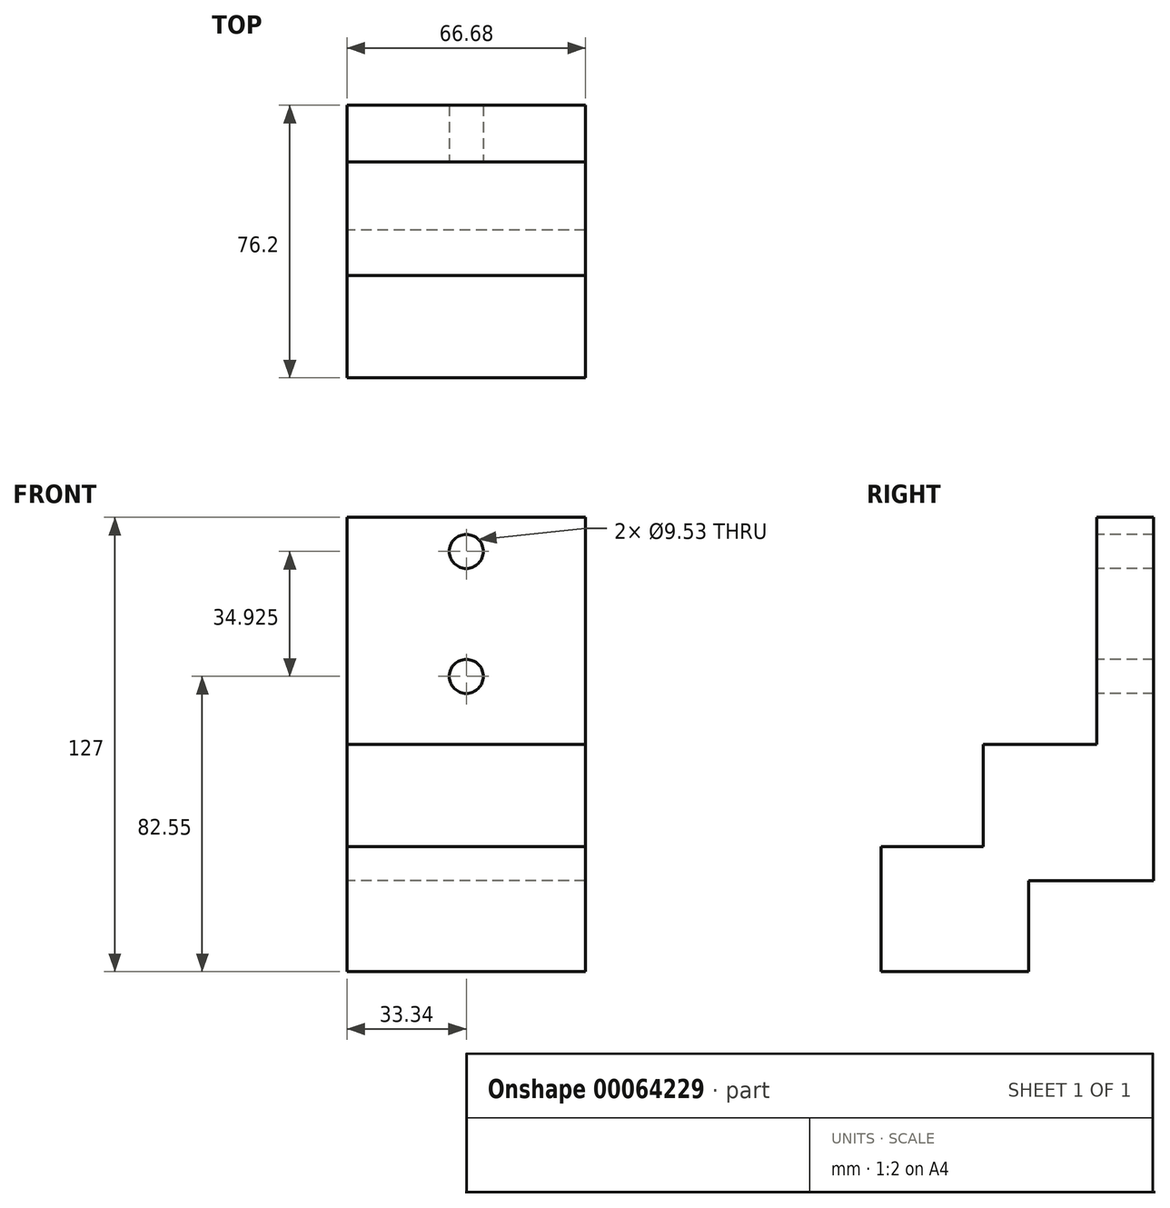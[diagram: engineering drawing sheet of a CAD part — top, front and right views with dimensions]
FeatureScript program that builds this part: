
annotation { "Feature Type Name" : "Feature", "Feature Type Description" : "" }
export const myFeature = defineFeature(function(context is Context, id is Id, definition is map)
    precondition{}
    {
        {
            var Q0;
            Q0=qCreatedBy(makeId("Right.planeOp"),FACE);
            var sketch = newSketch(context, id + "F0", { "sketchPlane" : qUnion([Q0])});
            skLineSegment(sketch, "E0", {"start": v(0, 0) * mm, "end": v(-41.28, 0) * mm});
            skLineSegment(sketch, "E1", {"start": v(-41.28, 0) * mm, "end": v(-41.28, 34.92) * mm});
            skLineSegment(sketch, "E2", {"start": v(-41.27, 34.92) * mm, "end": v(-12.7, 34.92) * mm});
            skLineSegment(sketch, "E3", {"start": v(-12.7, 34.92) * mm, "end": v(-12.7, 63.5) * mm});
            skLineSegment(sketch, "E4", {"start": v(-12.7, 63.5) * mm, "end": v(19.05, 63.5) * mm});
            skLineSegment(sketch, "E5", {"start": v(19.05, 63.5) * mm, "end": v(19.05, 127) * mm});
            skLineSegment(sketch, "E6", {"start": v(19.05, 127) * mm, "end": v(34.92, 127) * mm});
            skLineSegment(sketch, "E7", {"start": v(34.92, 127) * mm, "end": v(34.92, 25.4) * mm});
            skLineSegment(sketch, "E8", {"start": v(34.92, 25.4) * mm, "end": v(0, 25.4) * mm});
            skLineSegment(sketch, "E9", {"start": v(0, 25.4) * mm, "end": v(0, 0) * mm});
            skSolve(sketch);
        }
        {
            var Q0;
            Q0=qSketchRegion(id+"F0",true);
            extrude(context, id + "F1", {"entities" : qUnion([Q0]), "endBound" : BoundingType.SYMMETRIC, "depth" : 66.67 * mm});
        }
        {
            var Q0;
            Q0=makeQuery(id+"F1.opExtrude","SWEPT_FACE",FACE,{"disambiguationData":[OSD([sQuery(id+"F0.wireOp",EDGE,"E5")])]});
            var sketch = newSketch(context, id + "F2", { "sketchPlane" : qUnion([Q0])});
            skCircle(sketch, "E10", {"center": v(0, 117.47) * mm, "radius": 4.76 * mm});
            skPoint(sketch, "E10.centerSnap0", {"position": v(0, 63.5) * mm});
            skCircle(sketch, "E11", {"center": v(0, 82.55) * mm, "radius": 4.76 * mm});
            skSolve(sketch);
        }
        {
            var Q0;
            Q0=qSketchRegion(id+"F2",true);
            extrude(context, id + "F3", {"entities" : qUnion([Q0]), "operationType" : NewBodyOperationType.REMOVE, "endBound" : BoundingType.THROUGH_ALL, "oppositeDirection" : true, "depth" : 25.4 * mm});
        }
    });
